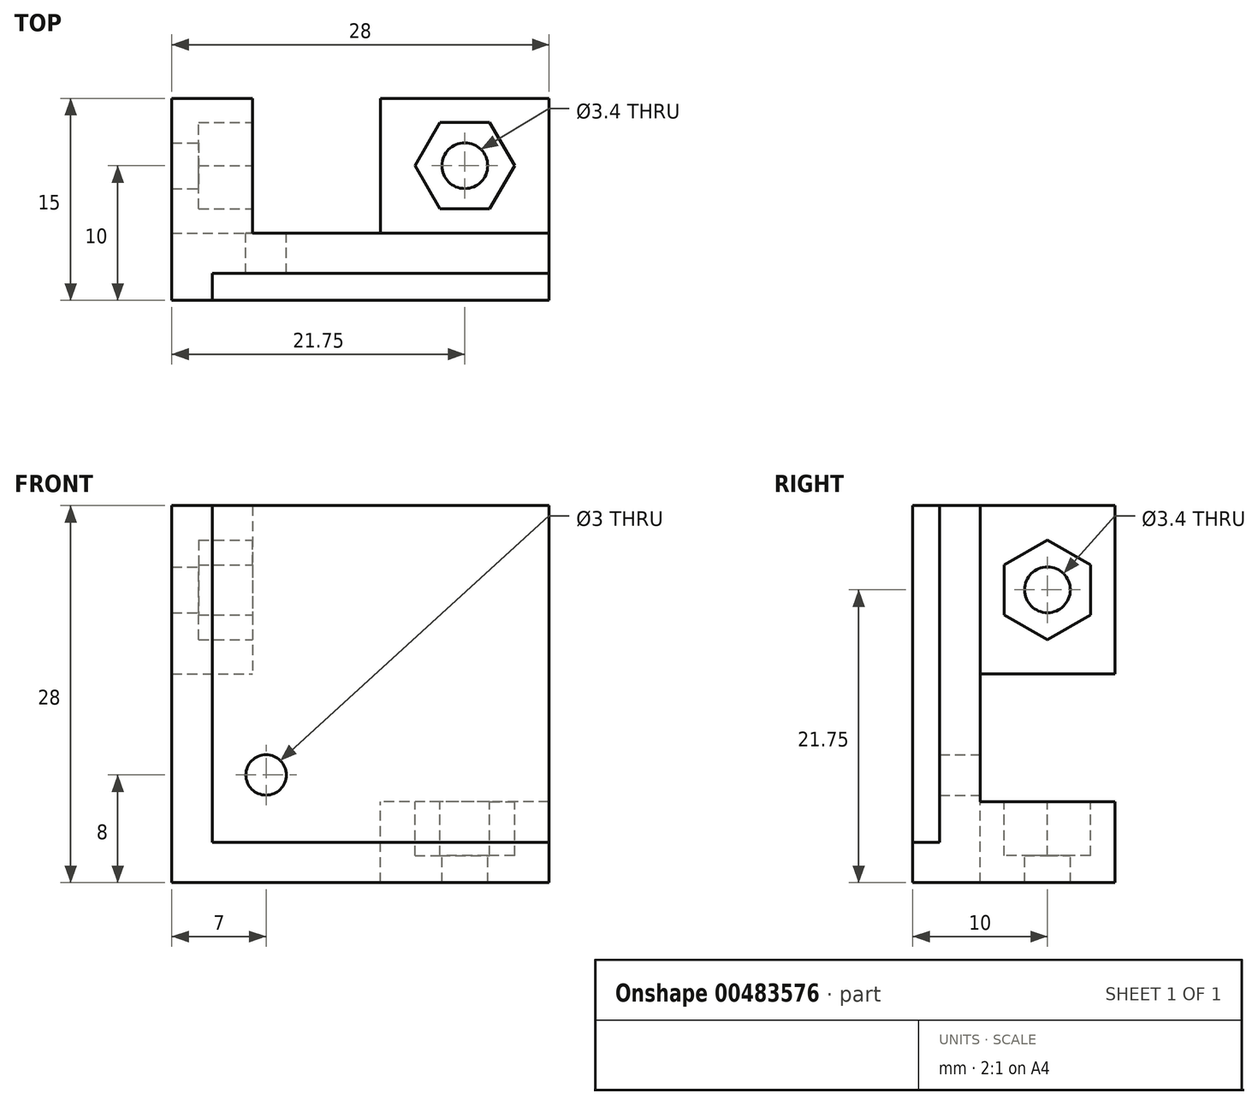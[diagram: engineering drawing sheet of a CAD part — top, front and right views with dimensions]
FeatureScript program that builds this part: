
annotation { "Feature Type Name" : "Feature", "Feature Type Description" : "" }
export const myFeature = defineFeature(function(context is Context, id is Id, definition is map)
    precondition{}
    {
        {
            var Q0;
            Q0=qCreatedBy(makeId("Front.planeOp"),FACE);
            var sketch = newSketch(context, id + "F0", { "sketchPlane" : qUnion([Q0])});
            skLineSegment(sketch, "E0.bottom", {"start": v(-12.5, 12.5) * mm, "end": v(12.5, 12.5) * mm});
            skLineSegment(sketch, "E0.top", {"start": v(-12.5, -12.5) * mm, "end": v(12.5, -12.5) * mm});
            skLineSegment(sketch, "E0.left", {"start": v(-12.5, 12.5) * mm, "end": v(-12.5, -12.5) * mm});
            skLineSegment(sketch, "E0.right", {"start": v(12.5, 12.5) * mm, "end": v(12.5, -12.5) * mm});
            skCircle(sketch, "E1", {"center": v(-8.5, -7.5) * mm, "radius": 1.5 * mm});
            skSolve(sketch);
        }
        {
            var Q0;
            Q0 = qSketchRegion(id + "F0", true);
            extrude(context, id + "F1", {"entities" : qUnion([Q0]), "depth" : 3 * mm});
        }
        {
            var Q0;
            Q0=qCreatedBy(makeId("Front.planeOp"),FACE);
            var sketch = newSketch(context, id + "F2", { "sketchPlane" : qUnion([Q0])});
            skLineSegment(sketch, "E2.0", {"start": v(-12.5, 12.5) * mm, "end": v(-12.5, -12.5) * mm});
            skLineSegment(sketch, "E3.0", {"start": v(-12.5, -12.5) * mm, "end": v(12.5, -12.5) * mm});
            skLineSegment(sketch, "E4", {"start": v(-12.5, 12.5) * mm, "end": v(-15.5, 12.5) * mm});
            skLineSegment(sketch, "E5", {"start": v(-15.5, -15.5) * mm, "end": v(-15.5, 12.5) * mm});
            skLineSegment(sketch, "E6", {"start": v(12.5, -12.5) * mm, "end": v(12.5, -15.5) * mm});
            skLineSegment(sketch, "E7", {"start": v(-15.5, -15.5) * mm, "end": v(12.5, -15.5) * mm});
            skSolve(sketch);
        }
        {
            var Q0;
            Q0 = qSketchRegion(id + "F2", true);
            extrude(context, id + "F3", {"entities" : qUnion([Q0]), "operationType" : NewBodyOperationType.ADD, "depth" : 5 * mm});
        }
        {
            var Q0;
            Q0=makeQuery(id+"F3.boolean.opBoolean","MERGE",FACE,{"derivedFrom":[makeQuery(id+"F1.opExtrude","CAP_FACE",FACE,{"disambiguationData":[OSD([sQuery(id+"F0.wireOp",EDGE,"E0.bottom"),sQuery(id+"F0.wireOp",EDGE,"E0.top"),sQuery(id+"F0.wireOp",EDGE,"E0.left"),sQuery(id+"F0.wireOp",EDGE,"E0.right"),sQuery(id+"F0.wireOp",EDGE,"E1")])],"isStart":true}),makeQuery(id+"F3.opExtrude","CAP_FACE",FACE,{"disambiguationData":[OSD([sQuery(id+"F2.wireOp",EDGE,"E2.0"),sQuery(id+"F2.wireOp",EDGE,"E3.0"),sQuery(id+"F2.wireOp",EDGE,"E4"),sQuery(id+"F2.wireOp",EDGE,"E5"),sQuery(id+"F2.wireOp",EDGE,"E6"),sQuery(id+"F2.wireOp",EDGE,"E7")])],"isStart":true})]});
            var sketch = newSketch(context, id + "F4", { "sketchPlane" : qUnion([Q0])});
            skLineSegment(sketch, "E8.bottom", {"start": v(15.5, 12.5) * mm, "end": v(9.5, 12.5) * mm});
            skLineSegment(sketch, "E8.top", {"start": v(15.5, 0) * mm, "end": v(9.5, 0) * mm});
            skLineSegment(sketch, "E8.left", {"start": v(15.5, 12.5) * mm, "end": v(15.5, 0) * mm});
            skLineSegment(sketch, "E8.right", {"start": v(9.5, 12.5) * mm, "end": v(9.5, 0) * mm});
            skLineSegment(sketch, "E9.bottom", {"start": v(-12.5, -15.5) * mm, "end": v(0, -15.5) * mm});
            skLineSegment(sketch, "E9.top", {"start": v(-12.5, -9.5) * mm, "end": v(0, -9.5) * mm});
            skLineSegment(sketch, "E9.left", {"start": v(-12.5, -15.5) * mm, "end": v(-12.5, -9.5) * mm});
            skLineSegment(sketch, "E9.right", {"start": v(0, -15.5) * mm, "end": v(0, -9.5) * mm});
            skSolve(sketch);
        }
        {
            var Q0;
            Q0 = qSketchRegion(id + "F4", true);
            extrude(context, id + "F5", {"entities" : qUnion([Q0]), "operationType" : NewBodyOperationType.ADD, "depth" : 10 * mm});
        }
        {
            var Q0;
            Q0=makeQuery(id+"F5.opExtrude","SWEPT_FACE",FACE,{"disambiguationData":[OSD([sQuery(id+"F4.wireOp",EDGE,"E9.top")])]});
            var sketch = newSketch(context, id + "F6", { "sketchPlane" : qUnion([Q0])});
            skCircle(sketch, "E10.cCircle", {"center": v(6.25, 5) * mm, "radius": 3.2 * mm, "construction": true});
            skLineSegment(sketch, "E10.0", {"start": v(9.95, 5) * mm, "end": v(8.1, 1.8) * mm});
            skLineSegment(sketch, "E10.1", {"start": v(8.1, 1.8) * mm, "end": v(4.4, 1.8) * mm});
            skLineSegment(sketch, "E10.2", {"start": v(4.4, 1.8) * mm, "end": v(2.55, 5) * mm});
            skLineSegment(sketch, "E10.3", {"start": v(2.55, 5) * mm, "end": v(4.4, 8.2) * mm});
            skLineSegment(sketch, "E10.4", {"start": v(4.4, 8.2) * mm, "end": v(8.1, 8.2) * mm});
            skLineSegment(sketch, "E10.5", {"start": v(8.1, 8.2) * mm, "end": v(9.95, 5) * mm});
            skPoint(sketch, "E10.0.midPoint", {"position": v(9.02, 3.4) * mm});
            skLineSegment(sketch, "E11", {"start": v(0, 0) * mm, "end": v(12.5, 10) * mm, "construction": true});
            skSolve(sketch);
        }
        {
            var Q0;
            Q0 = qSketchRegion(id + "F6", true);
            extrude(context, id + "F7", {"entities" : qUnion([Q0]), "operationType" : NewBodyOperationType.REMOVE, "oppositeDirection" : true, "depth" : 4 * mm});
        }
        {
            var Q0;
            Q0=makeQuery(id+"F5.opExtrude","SWEPT_FACE",FACE,{"disambiguationData":[OSD([sQuery(id+"F4.wireOp",EDGE,"E9.top")])]});
            var sketch = newSketch(context, id + "F8", { "sketchPlane" : qUnion([Q0])});
            skCircle(sketch, "E12", {"center": v(6.25, 5) * mm, "radius": 1.7 * mm});
            skLineSegment(sketch, "E13", {"start": v(2.55, 5) * mm, "end": v(9.95, 5) * mm, "construction": true});
            skSolve(sketch);
        }
        {
            var Q0;
            Q0 = qSketchRegion(id + "F8", true);
            extrude(context, id + "F9", {"entities" : qUnion([Q0]), "operationType" : NewBodyOperationType.REMOVE, "oppositeDirection" : true, "depth" : 25 * mm});
        }
        {
            var Q0;
            Q0=makeQuery(id+"F5.opExtrude","SWEPT_FACE",FACE,{"disambiguationData":[OSD([sQuery(id+"F4.wireOp",EDGE,"E8.right")])]});
            var sketch = newSketch(context, id + "F10", { "sketchPlane" : qUnion([Q0])});
            skLineSegment(sketch, "E14", {"start": v(0, 12.5) * mm, "end": v(10, 0) * mm, "construction": true});
            skCircle(sketch, "E15.cCircle", {"center": v(5, 6.25) * mm, "radius": 3.2 * mm, "construction": true});
            skLineSegment(sketch, "E15.0", {"start": v(8.2, 8.1) * mm, "end": v(8.2, 4.4) * mm});
            skLineSegment(sketch, "E15.1", {"start": v(8.2, 4.4) * mm, "end": v(5, 2.55) * mm});
            skLineSegment(sketch, "E15.2", {"start": v(5, 2.55) * mm, "end": v(1.8, 4.4) * mm});
            skLineSegment(sketch, "E15.3", {"start": v(1.8, 4.4) * mm, "end": v(1.8, 8.1) * mm});
            skLineSegment(sketch, "E15.4", {"start": v(1.8, 8.1) * mm, "end": v(5, 9.95) * mm});
            skLineSegment(sketch, "E15.5", {"start": v(5, 9.95) * mm, "end": v(8.2, 8.1) * mm});
            skPoint(sketch, "E15.0.midPoint", {"position": v(8.2, 6.25) * mm});
            skSolve(sketch);
        }
        {
            var Q0;
            Q0 = qSketchRegion(id + "F10", true);
            extrude(context, id + "F11", {"entities" : qUnion([Q0]), "operationType" : NewBodyOperationType.REMOVE, "oppositeDirection" : true, "depth" : 4 * mm});
        }
        {
            var Q0;
            Q0=makeQuery(id+"F5.opExtrude","SWEPT_FACE",FACE,{"disambiguationData":[OSD([sQuery(id+"F4.wireOp",EDGE,"E8.right")])]});
            var sketch = newSketch(context, id + "F12", { "sketchPlane" : qUnion([Q0])});
            skLineSegment(sketch, "E16", {"start": v(5, 9.95) * mm, "end": v(5, 2.55) * mm, "construction": true});
            skCircle(sketch, "E17", {"center": v(5, 6.25) * mm, "radius": 1.7 * mm});
            skSolve(sketch);
        }
        {
            var Q0;
            Q0 = qSketchRegion(id + "F12", true);
            extrude(context, id + "F13", {"entities" : qUnion([Q0]), "operationType" : NewBodyOperationType.REMOVE, "oppositeDirection" : true, "depth" : 25 * mm});
        }
    });
